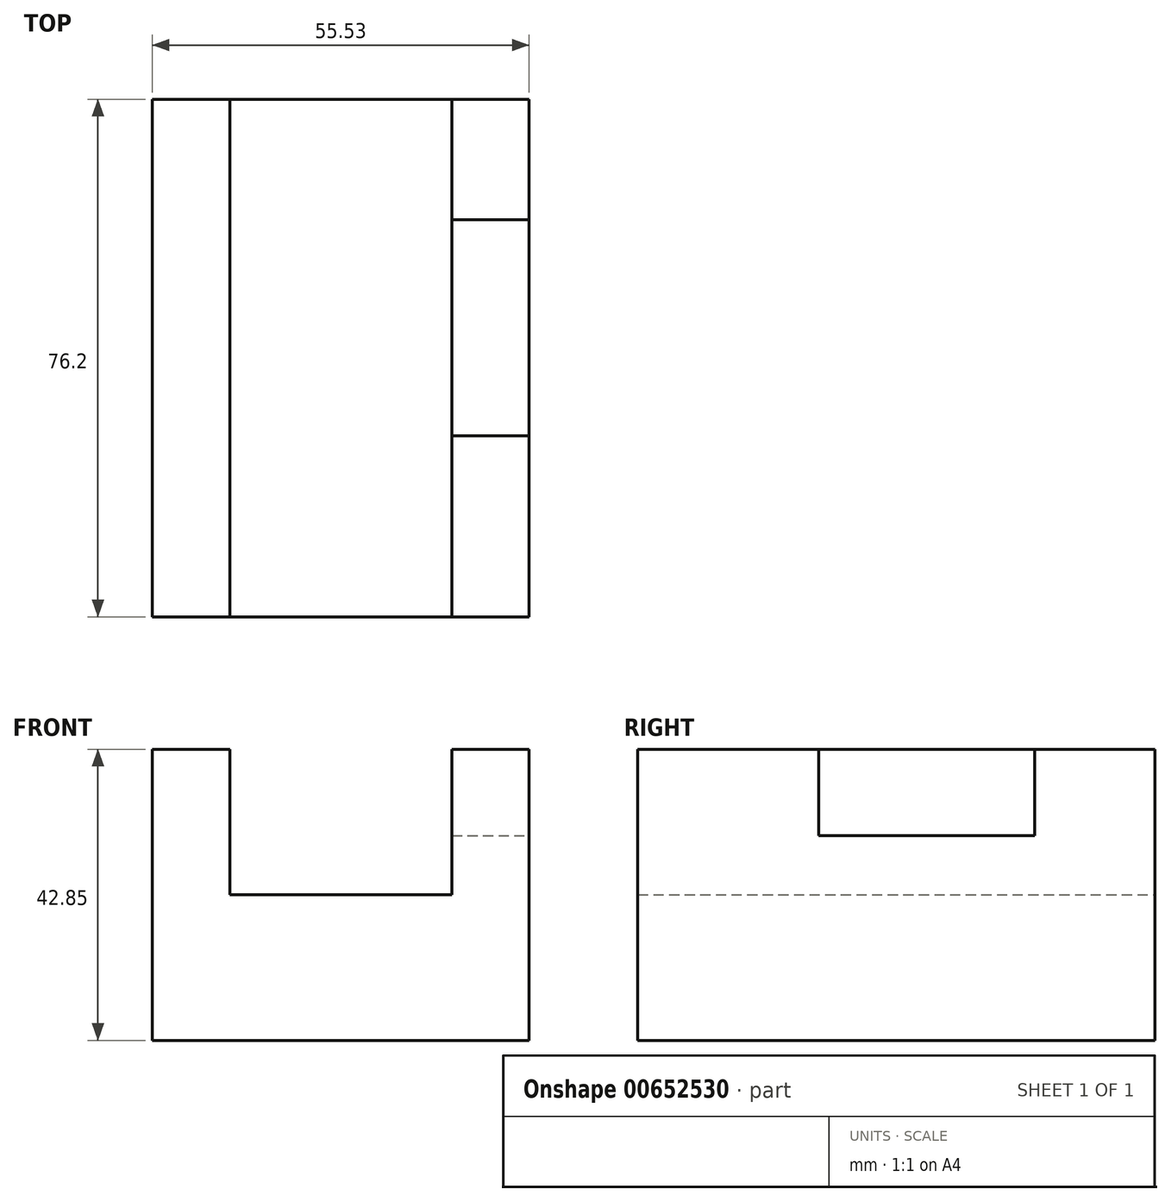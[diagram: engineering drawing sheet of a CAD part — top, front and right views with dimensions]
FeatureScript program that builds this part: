
annotation { "Feature Type Name" : "Feature", "Feature Type Description" : "" }
export const myFeature = defineFeature(function(context is Context, id is Id, definition is map)
    precondition{}
    {
        {
            var Q0;
            Q0=qCreatedBy(makeId("Front.planeOp"),FACE);
            var sketch = newSketch(context, id + "F0", { "sketchPlane" : qUnion([Q0])});
            skLineSegment(sketch, "E0.bottom", {"start": v(0, 0) * mm, "end": v(-55.53, 0) * mm});
            skLineSegment(sketch, "E0.top", {"start": v(0, 42.85) * mm, "end": v(-11.4, 42.85) * mm});
            skLineSegment(sketch, "E0.left", {"start": v(0, 0) * mm, "end": v(0, 42.85) * mm});
            skLineSegment(sketch, "E0.right", {"start": v(-55.53, 0) * mm, "end": v(-55.53, 42.85) * mm});
            skPoint(sketch, "E1.oppositeSnap0", {"position": v(0, 21.42) * mm});
            skLineSegment(sketch, "E1.top", {"start": v(-44.13, 21.42) * mm, "end": v(-11.4, 21.42) * mm});
            skLineSegment(sketch, "E1.left", {"start": v(-44.13, 42.85) * mm, "end": v(-44.13, 21.42) * mm});
            skLineSegment(sketch, "E1.right", {"start": v(-11.4, 42.85) * mm, "end": v(-11.4, 21.42) * mm});
            skLineSegment(sketch, "E2.trimOffspring", {"start": v(-44.13, 42.85) * mm, "end": v(-55.53, 42.85) * mm});
            skSolve(sketch);
        }
        {
            var Q0;
            Q0 = qSketchRegion(id + "F0", true);
            extrude(context, id + "F1", {"entities" : qUnion([Q0]), "depth" : 76.2 * mm, "offsetDistance" : 25.4 * mm});
        }
        {
            var Q0;
            Q0=makeQuery(id+"F1.opExtrude","SWEPT_FACE",FACE,{"disambiguationData":[OSD([sQuery(id+"F0.wireOp",EDGE,"E0.top")])]});
            var sketch = newSketch(context, id + "F2", { "sketchPlane" : qUnion([Q0])});
            skLineSegment(sketch, "E3.bottom", {"start": v(-11.4, -17.75) * mm, "end": v(0, -17.75) * mm});
            skLineSegment(sketch, "E3.top", {"start": v(-11.4, -49.54) * mm, "end": v(0, -49.54) * mm});
            skLineSegment(sketch, "E3.left", {"start": v(-11.4, -17.75) * mm, "end": v(-11.4, -49.54) * mm});
            skLineSegment(sketch, "E3.right", {"start": v(0, -17.75) * mm, "end": v(0, -49.54) * mm});
            skSolve(sketch);
        }
        {
            var Q0;
            Q0 = qSketchRegion(id + "F2", true);
            extrude(context, id + "F3", {"entities" : qUnion([Q0]), "operationType" : NewBodyOperationType.REMOVE, "oppositeDirection" : true, "depth" : 12.7 * mm, "offsetDistance" : 25.4 * mm});
        }
    });
